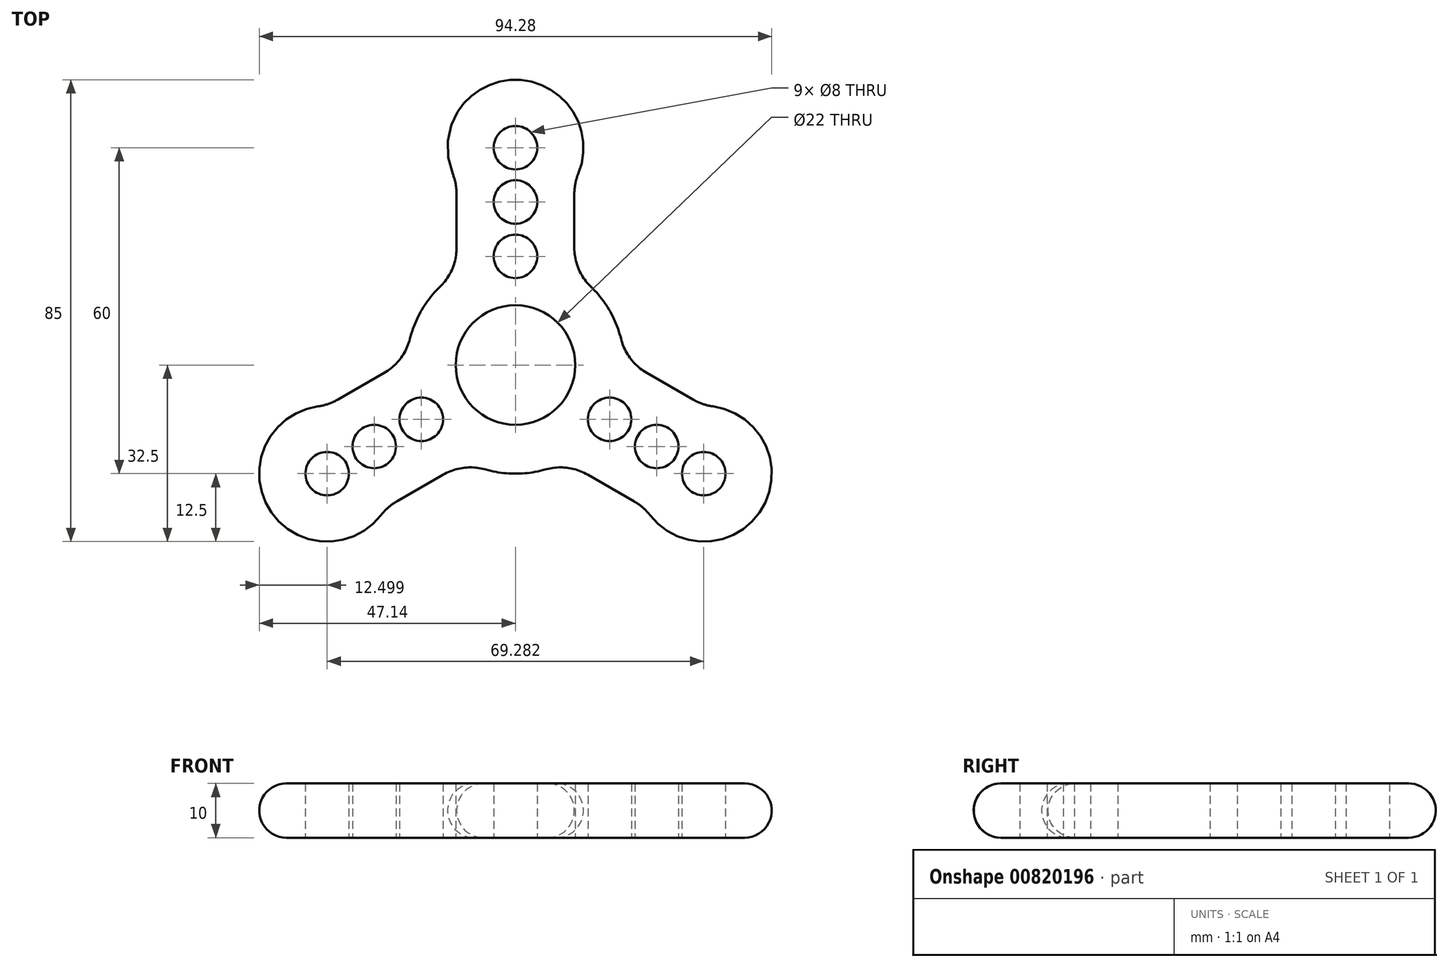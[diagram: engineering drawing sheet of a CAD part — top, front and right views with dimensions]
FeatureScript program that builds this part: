
annotation { "Feature Type Name" : "Feature", "Feature Type Description" : "" }
export const myFeature = defineFeature(function(context is Context, id is Id, definition is map)
    precondition{}
    {
        {
            var Q0;
            Q0=qCreatedBy(makeId("Top.planeOp"),FACE);
            var sketch = newSketch(context, id + "F0", { "sketchPlane" : qUnion([Q0])});
            skArc(sketch, "E0", {"start": v(-13.89, 14.4) * mm, "mid": v(-17.32, 10) * mm, "end": v(-19.4, 4.83) * mm});
            skCircle(sketch, "E1", {"center": v(0, 0) * mm, "radius": 11 * mm});
            skCircle(sketch, "E2", {"center": v(0, 0) * mm, "radius": 40 * mm, "construction": true});
            skLineSegment(sketch, "E3", {"start": v(-55.93, 32.3) * mm, "end": v(55.93, -32.3) * mm, "construction": true});
            skLineSegment(sketch, "E4", {"start": v(0, 58.64) * mm, "end": v(0, -62) * mm, "construction": true});
            skLineSegment(sketch, "E5", {"start": v(-40.83, -23.57) * mm, "end": v(40.83, 23.57) * mm, "construction": true});
            skArc(sketch, "E6", {"start": v(11.57, 35.27) * mm, "mid": v(0, 52.5) * mm, "end": v(-11.57, 35.27) * mm});
            skLineSegment(sketch, "E7", {"start": v(10.83, 31.5) * mm, "end": v(10.83, 21.59) * mm});
            skLineSegment(sketch, "E8", {"start": v(-10.83, 31.5) * mm, "end": v(-10.83, 21.59) * mm});
            skPoint(sketch, "E9.visualSharp", {"position": v(-10.83, 16.81) * mm});
            skArc(sketch, "E9.filletArc", {"start": v(-13.89, 14.4) * mm, "mid": v(-11.63, 17.68) * mm, "end": v(-10.83, 21.59) * mm});
            skPoint(sketch, "E10.visualSharp", {"position": v(-10.83, 33.76) * mm});
            skArc(sketch, "E10.filletArc", {"start": v(-10.83, 31.5) * mm, "mid": v(-11.02, 33.42) * mm, "end": v(-11.57, 35.27) * mm});
            skPoint(sketch, "E11.visualSharp", {"position": v(10.83, 33.76) * mm});
            skArc(sketch, "E11.filletArc", {"start": v(11.57, 35.27) * mm, "mid": v(11.02, 33.42) * mm, "end": v(10.83, 31.5) * mm});
            skPoint(sketch, "E12.visualSharp", {"position": v(10.83, 16.81) * mm});
            skArc(sketch, "E12.filletArc", {"start": v(10.83, 21.59) * mm, "mid": v(11.63, 17.68) * mm, "end": v(13.89, 14.4) * mm});
            skLineSegment(sketch, "E13.1.0", {"start": v(-32.69, -6.37) * mm, "end": v(-24.11, -1.42) * mm});
            skLineSegment(sketch, "E13.1.1", {"start": v(-21.86, -25.13) * mm, "end": v(-13.28, -20.17) * mm});
            skPoint(sketch, "E13.1.2", {"position": v(-19.98, 0.97) * mm});
            skArc(sketch, "E13.1.3", {"start": v(-36.33, -7.62) * mm, "mid": v(-45.47, -26.25) * mm, "end": v(-24.76, -27.66) * mm});
            skPoint(sketch, "E13.1.4", {"position": v(-23.82, -26.26) * mm});
            skPoint(sketch, "E13.1.5", {"position": v(-9.15, -17.79) * mm});
            skPoint(sketch, "E13.1.6", {"position": v(-34.65, -7.5) * mm});
            skArc(sketch, "E13.1.7", {"start": v(-24.11, -1.42) * mm, "mid": v(-21.12, 1.23) * mm, "end": v(-19.4, 4.83) * mm});
            skArc(sketch, "E13.1.8", {"start": v(-36.33, -7.62) * mm, "mid": v(-34.45, -7.17) * mm, "end": v(-32.69, -6.37) * mm});
            skArc(sketch, "E13.1.9", {"start": v(-5.52, -19.22) * mm, "mid": v(-9.5, -18.9) * mm, "end": v(-13.28, -20.17) * mm});
            skArc(sketch, "E13.1.10", {"start": v(-21.86, -25.13) * mm, "mid": v(-23.43, -26.25) * mm, "end": v(-24.76, -27.66) * mm});
            skLineSegment(sketch, "E13.2.0", {"start": v(21.86, -25.13) * mm, "end": v(13.28, -20.17) * mm});
            skLineSegment(sketch, "E13.2.1", {"start": v(32.69, -6.37) * mm, "end": v(24.11, -1.42) * mm});
            skPoint(sketch, "E13.2.2", {"position": v(9.15, -17.79) * mm});
            skArc(sketch, "E13.2.3", {"start": v(24.76, -27.66) * mm, "mid": v(45.47, -26.25) * mm, "end": v(36.33, -7.62) * mm});
            skPoint(sketch, "E13.2.4", {"position": v(34.65, -7.5) * mm});
            skPoint(sketch, "E13.2.5", {"position": v(19.98, 0.97) * mm});
            skPoint(sketch, "E13.2.6", {"position": v(23.82, -26.26) * mm});
            skArc(sketch, "E13.2.7", {"start": v(13.28, -20.17) * mm, "mid": v(9.5, -18.9) * mm, "end": v(5.52, -19.22) * mm});
            skArc(sketch, "E13.2.8", {"start": v(24.76, -27.66) * mm, "mid": v(23.43, -26.25) * mm, "end": v(21.86, -25.13) * mm});
            skArc(sketch, "E13.2.9", {"start": v(19.4, 4.83) * mm, "mid": v(21.12, 1.23) * mm, "end": v(24.11, -1.42) * mm});
            skArc(sketch, "E13.2.10", {"start": v(32.69, -6.37) * mm, "mid": v(34.45, -7.17) * mm, "end": v(36.33, -7.62) * mm});
            skArc(sketch, "E14.trimOffspring", {"start": v(-5.52, -19.22) * mm, "mid": v(0, -20) * mm, "end": v(5.52, -19.22) * mm});
            skArc(sketch, "E15.trimOffspring", {"start": v(19.4, 4.83) * mm, "mid": v(17.32, 10) * mm, "end": v(13.89, 14.4) * mm});
            skCircle(sketch, "E16", {"center": v(0, 40) * mm, "radius": 4 * mm});
            skCircle(sketch, "E17", {"center": v(0, 30) * mm, "radius": 4 * mm});
            skCircle(sketch, "E18", {"center": v(0, 20) * mm, "radius": 4 * mm});
            skCircle(sketch, "E19.1.0", {"center": v(-34.64, -20) * mm, "radius": 4 * mm});
            skCircle(sketch, "E19.1.1", {"center": v(-25.98, -15) * mm, "radius": 4 * mm});
            skCircle(sketch, "E19.1.2", {"center": v(-17.32, -10) * mm, "radius": 4 * mm});
            skCircle(sketch, "E19.2.0", {"center": v(34.64, -20) * mm, "radius": 4 * mm});
            skCircle(sketch, "E19.2.1", {"center": v(25.98, -15) * mm, "radius": 4 * mm});
            skCircle(sketch, "E19.2.2", {"center": v(17.32, -10) * mm, "radius": 4 * mm});
            skSolve(sketch);
        }
        {
            var Q0;
            Q0=makeQuery(id+"F0.imprint","IMPRINT",FACE,{"disambiguationData":[TD([[makeQuery(id+"F0.imprint","IMPRINT",EDGE,{"derivedFrom":sQuery(id+"F0.wireOp",EDGE,"E0")}),1.0]])]});
            extrude(context, id + "F1", {"entities" : qUnion([Q0]), "depth" : 10 * mm, "offsetDistance" : 25 * mm});
        }
        {
            var Q0;
            Q0=makeQuery(id+"F1.opExtrude","SWEPT_FACE",FACE,{"disambiguationData":[OSD([sQuery(id+"F0.wireOp",EDGE,"E6")])]});
            fillet(context, id + "F2", {"entities" : qUnion([Q0]), "radius" : 5 * mm, "tangentPropagation" : true, "allowEdgeOverflow" : false});
        }
    });
